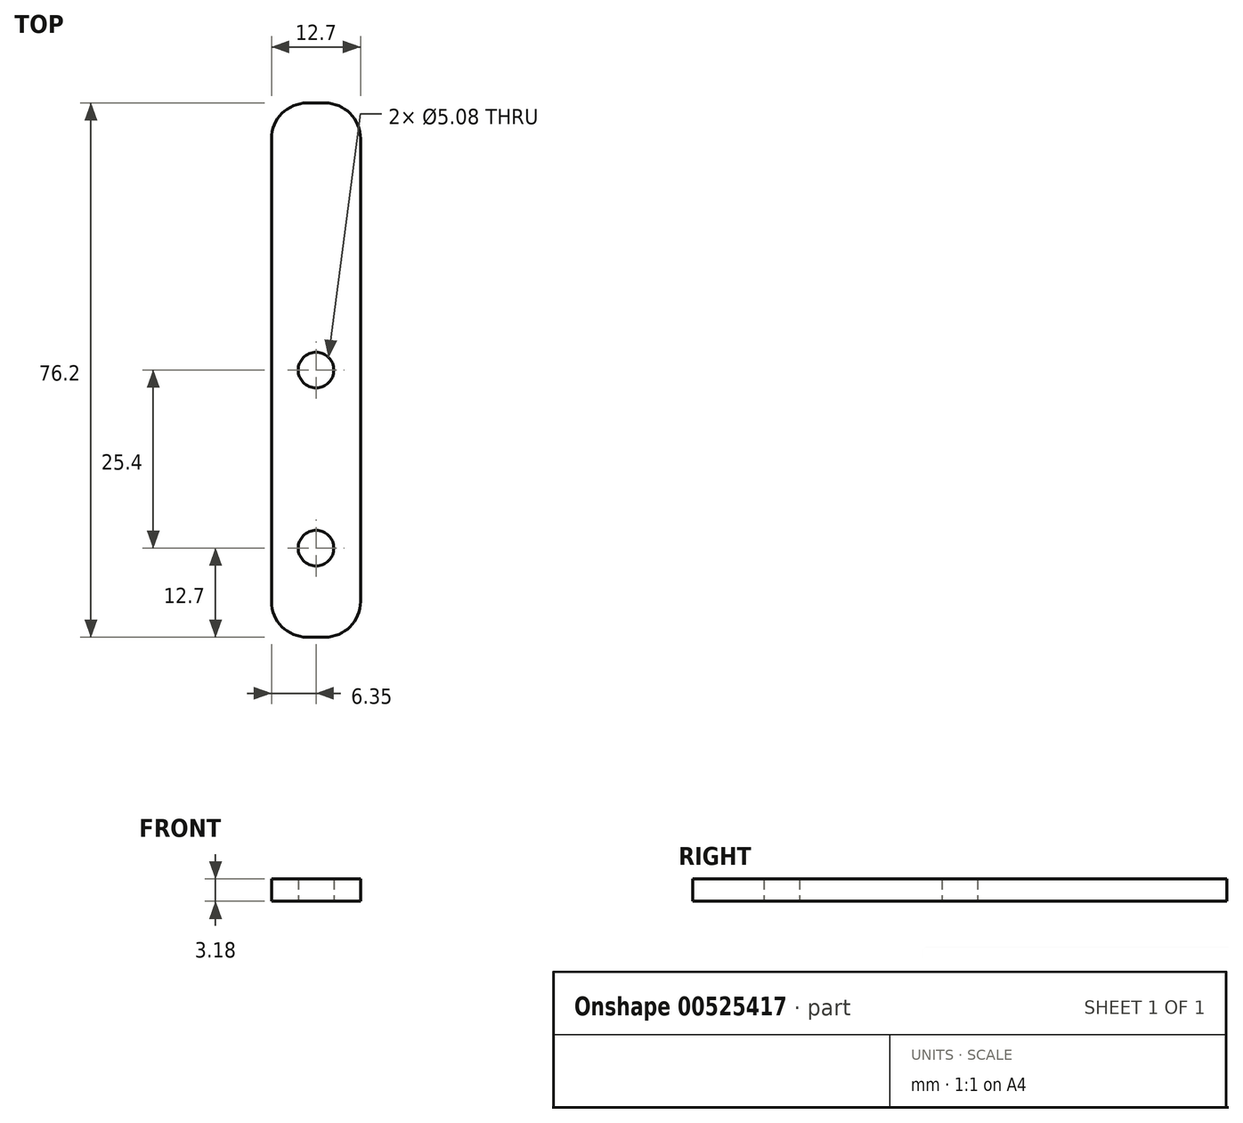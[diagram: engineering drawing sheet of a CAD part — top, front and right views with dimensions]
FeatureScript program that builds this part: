
annotation { "Feature Type Name" : "Feature", "Feature Type Description" : "" }
export const myFeature = defineFeature(function(context is Context, id is Id, definition is map)
    precondition{}
    {
        {
            var Q0;
            Q0=qCreatedBy(makeId("Top.planeOp"),FACE);
            var sketch = newSketch(context, id + "F0", { "sketchPlane" : qUnion([Q0])});
            skLineSegment(sketch, "E0.bottom", {"start": v(1.27, 38.1) * mm, "end": v(-1.27, 38.1) * mm});
            skLineSegment(sketch, "E0.top", {"start": v(1.27, -38.1) * mm, "end": v(-1.27, -38.1) * mm});
            skLineSegment(sketch, "E0.left", {"start": v(6.35, 33.02) * mm, "end": v(6.35, -33.02) * mm});
            skLineSegment(sketch, "E0.right", {"start": v(-6.35, 33.02) * mm, "end": v(-6.35, -33.02) * mm});
            skPoint(sketch, "E0.middle", {"position": v(0, 0) * mm});
            skCircle(sketch, "E1", {"center": v(0, -25.4) * mm, "radius": 2.54 * mm});
            skCircle(sketch, "E2", {"center": v(0, 0) * mm, "radius": 2.54 * mm});
            skPoint(sketch, "E3.visualSharp", {"position": v(6.35, 38.1) * mm});
            skArc(sketch, "E3.filletArc", {"start": v(6.35, 33.02) * mm, "mid": v(4.86, 36.61) * mm, "end": v(1.27, 38.1) * mm});
            skPoint(sketch, "E4.visualSharp", {"position": v(-6.35, 38.1) * mm});
            skArc(sketch, "E4.filletArc", {"start": v(-1.27, 38.1) * mm, "mid": v(-4.86, 36.61) * mm, "end": v(-6.35, 33.02) * mm});
            skPoint(sketch, "E5.visualSharp", {"position": v(6.35, -38.1) * mm});
            skArc(sketch, "E5.filletArc", {"start": v(1.27, -38.1) * mm, "mid": v(4.86, -36.61) * mm, "end": v(6.35, -33.02) * mm});
            skPoint(sketch, "E6.visualSharp", {"position": v(-6.35, -38.1) * mm});
            skArc(sketch, "E6.filletArc", {"start": v(-6.35, -33.02) * mm, "mid": v(-4.86, -36.61) * mm, "end": v(-1.27, -38.1) * mm});
            skSolve(sketch);
        }
        {
            var Q0;
            Q0=makeQuery(id+"F0.imprint","IMPRINT",FACE,{"disambiguationData":[TD([[makeQuery(id+"F0.imprint","IMPRINT",EDGE,{"derivedFrom":sQuery(id+"F0.wireOp",EDGE,"E0.bottom")}),1.0]])]});
            extrude(context, id + "F1", {"entities" : qUnion([Q0]), "depth" : 3.17 * mm, "offsetDistance" : 25.4 * mm});
        }
    });
